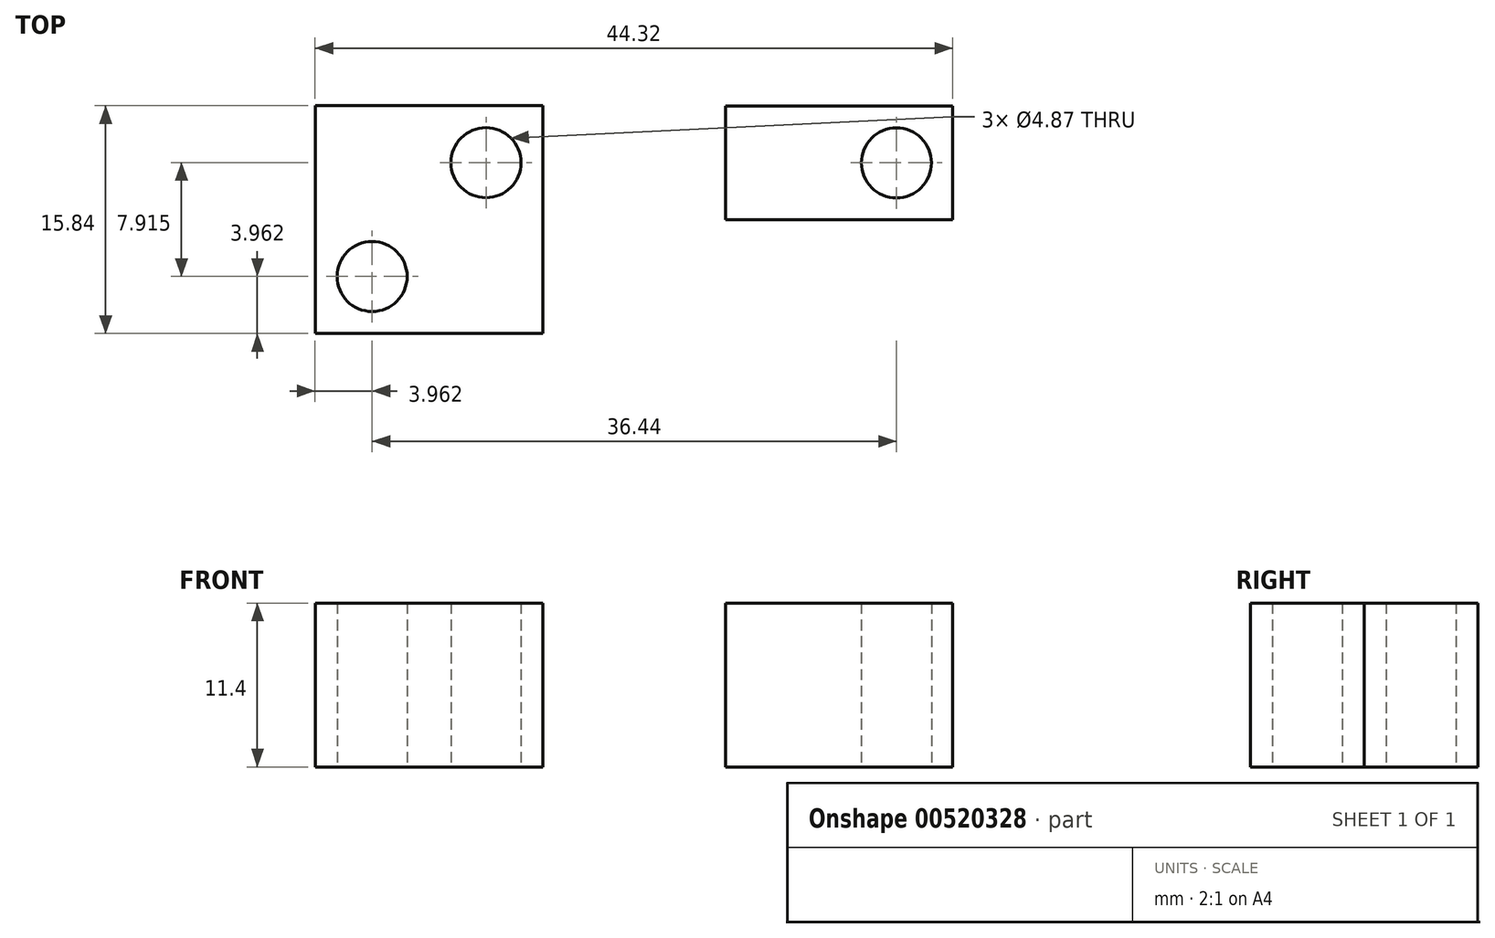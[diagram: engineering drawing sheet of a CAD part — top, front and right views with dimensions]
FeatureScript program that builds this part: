
annotation { "Feature Type Name" : "Feature", "Feature Type Description" : "" }
export const myFeature = defineFeature(function(context is Context, id is Id, definition is map)
    precondition{}
    {
        {
            var Q0;
            Q0=qCreatedBy(makeId("Top.planeOp"),FACE);
            var sketch = newSketch(context, id + "F0", { "sketchPlane" : qUnion([Q0])});
            skLineSegment(sketch, "E0.bottom", {"start": v(7.92, -7.91) * mm, "end": v(-7.91, -7.91) * mm});
            skLineSegment(sketch, "E0.top", {"start": v(7.92, 7.92) * mm, "end": v(-7.91, 7.92) * mm});
            skLineSegment(sketch, "E0.left", {"start": v(7.92, -7.91) * mm, "end": v(7.92, 7.92) * mm});
            skLineSegment(sketch, "E0.right", {"start": v(-7.91, -7.91) * mm, "end": v(-7.91, 7.92) * mm});
            skPoint(sketch, "E0.middle", {"position": v(0, 0) * mm});
            skCircle(sketch, "E1", {"center": v(3.96, -3.96) * mm, "radius": 2.44 * mm});
            skCircle(sketch, "E2.MirrorC", {"center": v(3.96, 3.96) * mm, "radius": 2.44 * mm});
            skCircle(sketch, "E3.MirrorC", {"center": v(-3.96, 3.96) * mm, "radius": 2.44 * mm});
            skCircle(sketch, "E4.MirrorC", {"center": v(-3.96, -3.96) * mm, "radius": 2.44 * mm});
            skLineSegment(sketch, "E5.bottom", {"start": v(20.6, 7.9) * mm, "end": v(36.4, 7.9) * mm});
            skLineSegment(sketch, "E5.left", {"start": v(20.6, 7.9) * mm, "end": v(20.6, 0) * mm});
            skLineSegment(sketch, "E5.right", {"start": v(36.4, 7.9) * mm, "end": v(36.4, 0) * mm});
            skPoint(sketch, "E5.middle", {"position": v(28.5, 0) * mm});
            skLineSegment(sketch, "E6.bottom", {"start": v(20.6, 7.9) * mm, "end": v(22.1, 7.9) * mm});
            skLineSegment(sketch, "E6.left", {"start": v(20.6, 7.9) * mm, "end": v(20.6, 6.4) * mm});
            skLineSegment(sketch, "E7", {"start": v(22.1, 7.9) * mm, "end": v(26.97, 7.9) * mm});
            skLineSegment(sketch, "E8", {"start": v(26.97, 7.9) * mm, "end": v(30.07, 7.9) * mm});
            skLineSegment(sketch, "E9", {"start": v(30.07, 7.9) * mm, "end": v(28.52, 7.9) * mm});
            skCircle(sketch, "E10", {"center": v(24.53, 3.97) * mm, "radius": 2.43 * mm});
            skCircle(sketch, "E11.MirrorC", {"center": v(32.48, 3.94) * mm, "radius": 2.43 * mm});
            skLineSegment(sketch, "E12", {"start": v(20.6, 0) * mm, "end": v(36.4, 0) * mm});
            skPoint(sketch, "E13.orphan", {"position": v(36.4, -7.9) * mm});
            skPoint(sketch, "E14.orphan", {"position": v(20.6, -7.9) * mm});
            skPoint(sketch, "E15.orphan", {"position": v(24.53, 7.9) * mm});
            skPoint(sketch, "E16.orphan", {"position": v(0, 7.92) * mm});
            skPoint(sketch, "E17.end.orphan", {"position": v(0, -7.91) * mm});
            skPoint(sketch, "E18.orphan", {"position": v(-7.91, 0) * mm});
            skPoint(sketch, "E19.start.orphan", {"position": v(7.92, 0) * mm});
            skSolve(sketch);
        }
        {
            var Q0;
            Q0 = qSketchRegion(id + "F0", true);
            extrude(context, id + "F1", {"entities" : qUnion([Q0]), "depth" : 9.6 * mm, "offsetDistance" : 25 * mm});
        }
        {
            var Q0;
            Q0=makeQuery(id+"F0.imprint","IMPRINT",FACE,{"disambiguationData":[TD([[makeQuery(id+"F0.imprint","IMPRINT",EDGE,{"derivedFrom":sQuery(id+"F0.wireOp",EDGE,"E3.MirrorC")}),1.0]])]});
            var Q1;
            Q1=makeQuery(id+"F0.imprint","IMPRINT",FACE,{"disambiguationData":[TD([[makeQuery(id+"F0.imprint","IMPRINT",EDGE,{"derivedFrom":sQuery(id+"F0.wireOp",EDGE,"E2.MirrorC")}),-1.0]])]});
            var Q2;
            Q2=makeQuery(id+"F0.imprint","IMPRINT",FACE,{"disambiguationData":[TD([[makeQuery(id+"F0.imprint","IMPRINT",EDGE,{"derivedFrom":sQuery(id+"F0.wireOp",EDGE,"E1")}),1.0]])]});
            var Q3;
            Q3=makeQuery(id+"F0.imprint","IMPRINT",FACE,{"disambiguationData":[TD([[makeQuery(id+"F0.imprint","IMPRINT",EDGE,{"derivedFrom":sQuery(id+"F0.wireOp",EDGE,"E10")}),1.0]])]});
            var Q4;
            Q4=makeQuery(id+"F0.imprint","IMPRINT",FACE,{"disambiguationData":[TD([[makeQuery(id+"F0.imprint","IMPRINT",EDGE,{"derivedFrom":sQuery(id+"F0.wireOp",EDGE,"E11.MirrorC")}),-1.0]])]});
            var Q5;
            Q5=makeQuery(id+"F0.imprint","IMPRINT",FACE,{"disambiguationData":[TD([[makeQuery(id+"F0.imprint","IMPRINT",EDGE,{"derivedFrom":sQuery(id+"F0.wireOp",EDGE,"E4.MirrorC")}),-1.0]])]});
            extrude(context, id + "F2", {"entities" : qUnion([Q0, Q1, Q2, Q3, Q4, Q5]), "operationType" : NewBodyOperationType.ADD, "depth" : 11.4 * mm, "offsetDistance" : 25 * mm});
        }
    });
